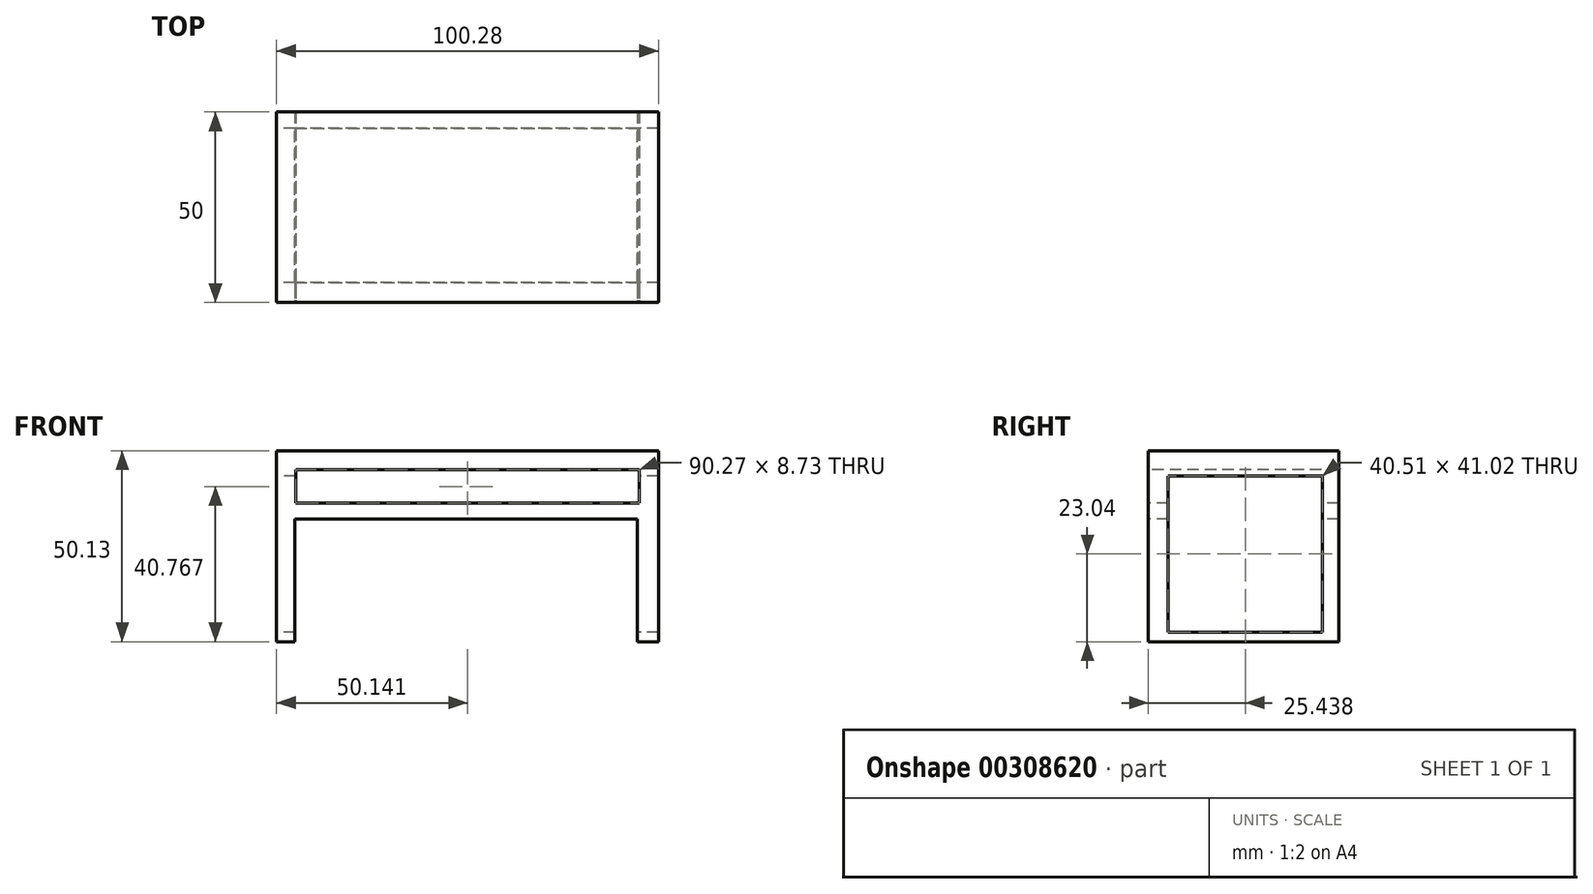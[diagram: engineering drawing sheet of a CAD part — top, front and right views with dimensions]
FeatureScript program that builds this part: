
annotation { "Feature Type Name" : "Feature", "Feature Type Description" : "" }
export const myFeature = defineFeature(function(context is Context, id is Id, definition is map)
    precondition{}
    {
        {
            var Q0;
            Q0=qCreatedBy(makeId("Front.planeOp"),FACE);
            var sketch = newSketch(context, id + "F0", { "sketchPlane" : qUnion([Q0])});
            skLineSegment(sketch, "E0.bottom", {"start": v(-65.84, 56.46) * mm, "end": v(34.44, 56.46) * mm});
            skLineSegment(sketch, "E0.top", {"start": v(-65.84, 6.33) * mm, "end": v(34.44, 6.33) * mm});
            skLineSegment(sketch, "E0.left", {"start": v(-65.84, 56.46) * mm, "end": v(-65.84, 6.33) * mm});
            skLineSegment(sketch, "E0.right", {"start": v(34.44, 56.46) * mm, "end": v(34.44, 6.33) * mm});
            skSolve(sketch);
        }
        {
            var Q0;
            Q0=qSketchRegion(id+"F0",true);
            extrude(context, id + "F1", {"entities" : qUnion([Q0]), "depth" : 50 * mm});
        }
        {
            var Q0;
            Q0=makeQuery(id+"F1.opExtrude","CAP_FACE",FACE,{"disambiguationData":[OSD([sQuery(id+"F0.wireOp",EDGE,"E0.bottom"),sQuery(id+"F0.wireOp",EDGE,"E0.top"),sQuery(id+"F0.wireOp",EDGE,"E0.left"),sQuery(id+"F0.wireOp",EDGE,"E0.right")])],"isStart":false});
            var sketch = newSketch(context, id + "F2", { "sketchPlane" : qUnion([Q0])});
            skLineSegment(sketch, "E1.bottom", {"start": v(-60.84, 51.46) * mm, "end": v(29.44, 51.46) * mm});
            skLineSegment(sketch, "E1.top", {"start": v(-60.84, 42.73) * mm, "end": v(29.44, 42.73) * mm});
            skLineSegment(sketch, "E1.left", {"start": v(-60.84, 51.46) * mm, "end": v(-60.84, 42.73) * mm});
            skLineSegment(sketch, "E1.right", {"start": v(29.44, 51.46) * mm, "end": v(29.44, 42.73) * mm});
            skSolve(sketch);
        }
        {
            var Q0;
            Q0=makeQuery(id+"F2.imprint","IMPRINT",FACE,{"disambiguationData":[TD([[makeQuery(id+"F2.imprint","IMPRINT",EDGE,{"derivedFrom":sQuery(id+"F2.wireOp",EDGE,"E1.bottom")}),-1.0]])]});
            extrude(context, id + "F3", {"entities" : qUnion([Q0]), "operationType" : NewBodyOperationType.REMOVE, "endBound" : BoundingType.THROUGH_ALL, "oppositeDirection" : true, "depth" : 25 * mm});
        }
        {
            var Q0;
            Q0=makeQuery(id+"F1.opExtrude","SWEPT_FACE",FACE,{"disambiguationData":[OSD([sQuery(id+"F0.wireOp",EDGE,"E0.left")])]});
            var sketch = newSketch(context, id + "F4", { "sketchPlane" : qUnion([Q0])});
            skSolve(sketch);
        }
        {
            var Q0;
            {var subQ0=sQuery(id+"F0.wireOp",EDGE,"E0.left");Q0=makeQuery(id+"F4.imprint","IMPRINT",FACE,{"disambiguationData":[TD([[makeQuery(id+"F4.imprint","IMPRINT",EDGE,{"derivedFrom":makeQuery(id+"F1.opExtrude","CAP_EDGE",EDGE,{"disambiguationData":[OSD([subQ0])],"isStart":true})}),1.0]])]});}
            var sketch = newSketch(context, id + "F5", { "sketchPlane" : qUnion([Q0])});
            skLineSegment(sketch, "E2.bottom", {"start": v(4.3, 49.88) * mm, "end": v(44.82, 49.88) * mm});
            skLineSegment(sketch, "E2.top", {"start": v(4.3, 8.86) * mm, "end": v(44.82, 8.86) * mm});
            skLineSegment(sketch, "E2.left", {"start": v(4.3, 49.88) * mm, "end": v(4.3, 8.86) * mm});
            skLineSegment(sketch, "E2.right", {"start": v(44.82, 49.88) * mm, "end": v(44.82, 8.86) * mm});
            skSolve(sketch);
        }
        {
            var Q0;
            Q0=qSketchRegion(id+"F5",true);
            extrude(context, id + "F6", {"entities" : qUnion([Q0]), "operationType" : NewBodyOperationType.REMOVE, "endBound" : BoundingType.THROUGH_ALL, "oppositeDirection" : true, "depth" : 25 * mm});
        }
        {
            var Q0;
            Q0=makeQuery(id+"F1.opExtrude","CAP_FACE",FACE,{"disambiguationData":[OSD([sQuery(id+"F0.wireOp",EDGE,"E0.bottom"),sQuery(id+"F0.wireOp",EDGE,"E0.top"),sQuery(id+"F0.wireOp",EDGE,"E0.left"),sQuery(id+"F0.wireOp",EDGE,"E0.right")])],"isStart":false});
            var sketch = newSketch(context, id + "F7", { "sketchPlane" : qUnion([Q0])});
            skLineSegment(sketch, "E3.bottom", {"start": v(-61.02, 38.49) * mm, "end": v(28.87, 38.49) * mm});
            skLineSegment(sketch, "E3.top", {"start": v(-61.02, 6.33) * mm, "end": v(28.87, 6.33) * mm});
            skLineSegment(sketch, "E3.left", {"start": v(-61.02, 38.49) * mm, "end": v(-61.02, 6.33) * mm});
            skLineSegment(sketch, "E3.right", {"start": v(28.87, 38.49) * mm, "end": v(28.87, 6.33) * mm});
            skSolve(sketch);
        }
        {
            var Q0;
            Q0=qSketchRegion(id+"F7",true);
            extrude(context, id + "F8", {"entities" : qUnion([Q0]), "operationType" : NewBodyOperationType.REMOVE, "endBound" : BoundingType.THROUGH_ALL, "oppositeDirection" : true, "depth" : 25 * mm});
        }
    });
